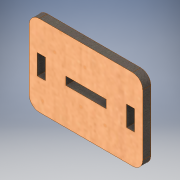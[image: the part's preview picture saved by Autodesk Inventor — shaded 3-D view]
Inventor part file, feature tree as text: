
AUTODESK INVENTOR PART (.ipt)
format: ipt  version: 2019 (Build 230136000, 136)  size: 149,504 bytes
history: native  units: mm
features: other x1, extrude x1, sketch x1
ambient origin geometry x8: Origin, YZ Plane, XZ Plane, XY Plane, X Axis, Y Axis, Z Axis, Center Point
bodies: Body1 (feature_tree)
feature tree (3):
  other  "Твердое тело1"
  extrude  "Выдавливание1"  Depth=4.0mm
  sketch  "Эскиз1"
